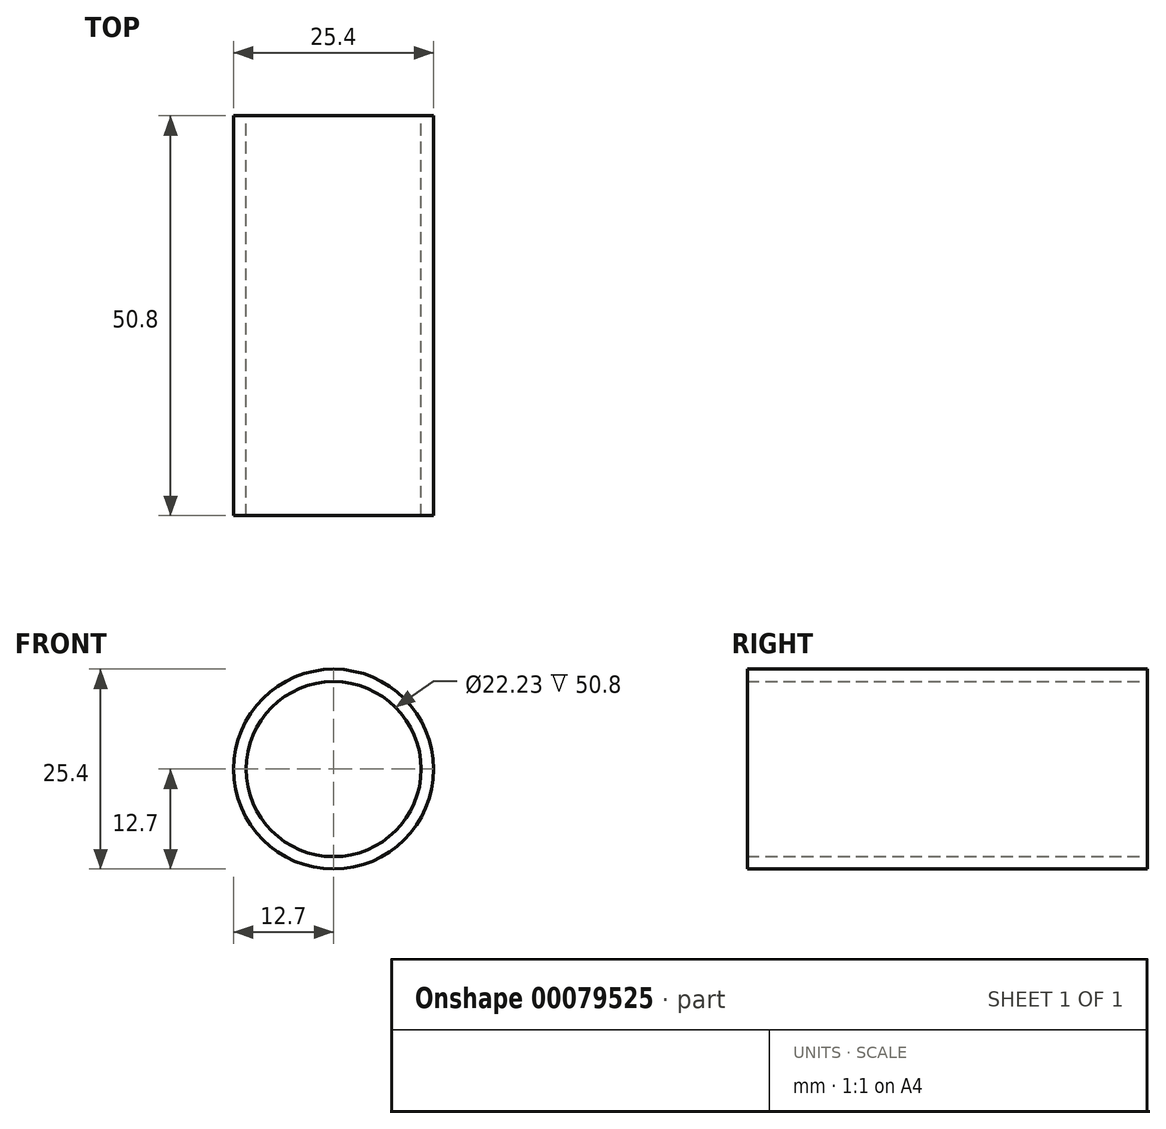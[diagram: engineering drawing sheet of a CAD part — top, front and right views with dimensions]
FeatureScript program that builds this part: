
annotation { "Feature Type Name" : "Feature", "Feature Type Description" : "" }
export const myFeature = defineFeature(function(context is Context, id is Id, definition is map)
    precondition{}
    {
        {
            var Q0;
            Q0=qCreatedBy(makeId("Front.planeOp"),FACE);
            var sketch = newSketch(context, id + "F0", { "sketchPlane" : qUnion([Q0])});
            skCircle(sketch, "E0", {"center": v(0, 0) * mm, "radius": 12.7 * mm});
            skCircle(sketch, "E1", {"center": v(0, 0) * mm, "radius": 11.11 * mm});
            skSolve(sketch);
        }
        {
            var Q0;
            Q0=makeQuery(id+"F0.imprint","IMPRINT",FACE,{"disambiguationData":[TD([[makeQuery(id+"F0.imprint","IMPRINT",EDGE,{"derivedFrom":sQuery(id+"F0.wireOp",EDGE,"E0")}),1.0]])]});
            extrude(context, id + "F1", {"entities" : qUnion([Q0]), "depth" : 50.8 * mm});
        }
    });
